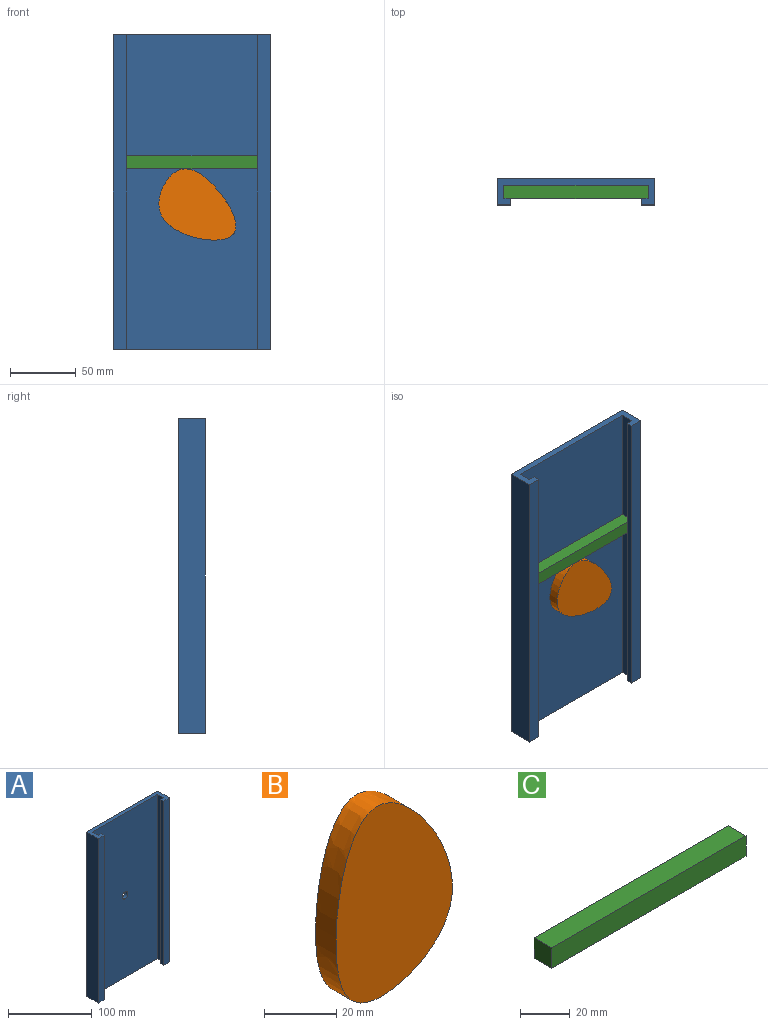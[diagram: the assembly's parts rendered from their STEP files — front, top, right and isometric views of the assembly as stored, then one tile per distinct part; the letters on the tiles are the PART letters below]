
ASSEMBLY  parts=3 mates=2
PART A: 15 faces, bbox 120x20x240 mm
  f0: plane 240x5mm, normal (1,0,0), area 1200mm2, adj f1,f3,f8,f13
  f1: plane 120x20mm, normal (0,0,-1), area 800mm2, adj f0,f2,f4,f5,f6,f7,f8,f9
  f2: plane 240x5mm, normal (-1,0,0), area 1200mm2, adj f1,f3,f6,f11
  f3: plane 120x20mm, normal (0,0,1), area 800mm2, adj f0,f2,f4,f5,f6,f7,f8,f9
  f4: plane 240x110mm, normal (0,-1,0), area 26321.5mm2, adj f1,f3,f5,f7,f14
  f5: plane 240x10mm, normal (-1,0,0), area 2400mm2, adj f1,f3,f4,f6
  f6: plane 240x5mm, normal (0,1,0), area 1200mm2, adj f1,f2,f3,f5
  f7: plane 240x10mm, normal (1,0,0), area 2400mm2, adj f1,f3,f4,f8
  f8: plane 240x5mm, normal (0,1,0), area 1200mm2, adj f0,f1,f3,f7
  f9: plane 240x120mm, normal (0,1,0), area 28721.5mm2, adj f1,f3,f10,f12,f14
  f10: plane 240x20mm, normal (1,0,0), area 4800mm2, adj f1,f3,f9,f11
  f11: plane 240x10mm, normal (0,-1,0), area 2400mm2, adj f1,f2,f3,f10
  f12: plane 240x20mm, normal (-1,0,0), area 4800mm2, adj f1,f3,f9,f13
  f13: plane 240x10mm, normal (0,-1,0), area 2400mm2, adj f0,f1,f3,f12
  f14: cylinder r=5mm len=10mm, axis (0,-1,0), area 157.1mm2, adj f4,f9
PART B: 5 faces, bbox 51x15x69 mm
  f0: plane 10x10mm, normal (0,1,0), area 78.5mm2, adj f1
  f1: cylinder r=5mm len=10mm, axis (0,-1,0), area 219.9mm2, adj f0,f4
  f2: extruded ~65.1x45.46mm, area 1405.8mm2, adj f3,f4
  f3: plane 69.02x51.05mm, normal (0,-1,0), area 2271.9mm2, adj f2
  f4: plane 69.02x51.05mm, normal (0,1,0), area 2193.4mm2, adj f1,f2
PART C: 6 faces, bbox 110x10x10 mm
  f0: plane 10x10mm, normal (1,0,0), area 100mm2, adj f1,f2,f4,f5
  f1: plane 110x10mm, normal (0,0,1), area 1100mm2, adj f0,f3,f4,f5
  f2: plane 110x10mm, normal (0,0,-1), area 1100mm2, adj f0,f3,f4,f5
  f3: plane 10x10mm, normal (-1,0,0), area 100mm2, adj f1,f2,f4,f5
  f4: plane 110x10mm, normal (0,1,0), area 1100mm2, adj f0,f1,f2,f3
  f5: plane 110x10mm, normal (0,-1,0), area 1100mm2, adj f0,f1,f2,f3
PLACE A at identity fixed
PLACE B rot(axis=(0,1,0),135.6deg) t=(78.65,0,76.9)mm
PLACE C t=(0,0,-92.37)mm
MATE slider A.f3 <-> C.f1  axis (0,0,1) through (-55,2,120)mm
MATE revolute A.f14 <-> B.f1  axis (0,1,0) through (0,7,0)mm
